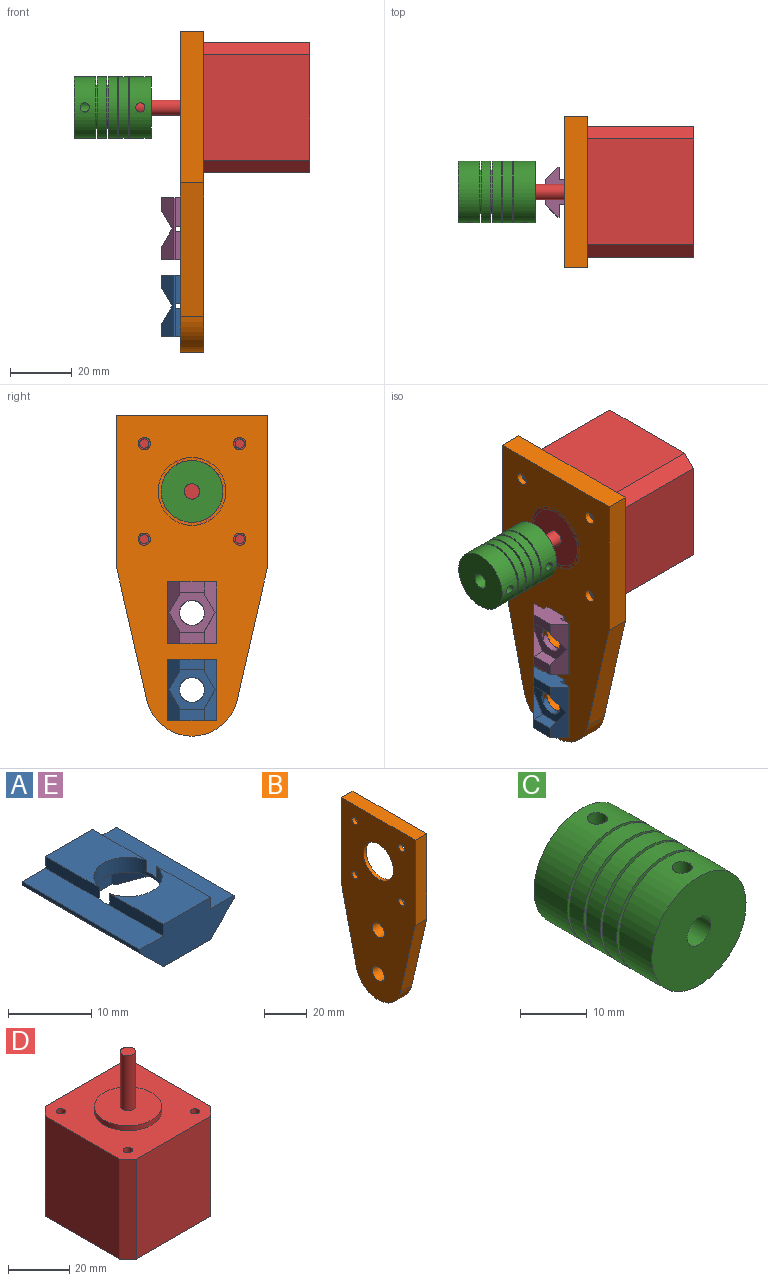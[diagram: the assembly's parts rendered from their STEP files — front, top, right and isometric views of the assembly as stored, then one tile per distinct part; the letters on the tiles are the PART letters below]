
ASSEMBLY  parts=5 mates=4
PART A: 24 faces, bbox 16x20x6.2 mm
  f0: plane 20x0.5mm, normal (-1,0,0), area 10mm2, adj f2,f3,f17,f23
  f1: plane 20x0.5mm, normal (1,0,0), area 10mm2, adj f2,f3,f20,f22
  f2: plane 16x6.2mm, normal (0,1,0), area 69.6mm2, adj f0,f1,f7,f10,f16,f17,f19,f20
  f3: plane 16x6.2mm, normal (0,-1,0), area 69.6mm2, adj f0,f1,f6,f9,f17,f18,f20,f21
  f4: plane 6.5x4mm, normal (-0.87,-0.5,0), area 17.7mm2, adj f5,f7,f14,f15,f22
  f5: plane 6.5x4mm, normal (-0.87,0.5,0), area 17.7mm2, adj f4,f6,f11,f15,f22
  f6: plane 8x3.93mm, normal (0,0,-1), area 28.1mm2, adj f3,f5,f11,f12,f22,f23
  f7: plane 8x3.93mm, normal (0,0,-1), area 28.1mm2, adj f2,f4,f13,f14,f22,f23
  f8: cylinder r=4.1mm len=8.2mm, axis (0,0,-1), area 50.5mm2, adj f9,f10,f15,f16,f17,f18,f19,f20
  f9: plane 9.1x8mm, normal (0,0,1), area 53.7mm2, adj f3,f8,f18,f21
  f10: plane 9.1x8mm, normal (0,0,1), area 53.7mm2, adj f2,f8,f16,f19
  f11: plane 7.51x4mm, normal (0,1,0), area 30mm2, adj f5,f6,f12,f15
  f12: plane 6.5x4mm, normal (0.87,0.5,0), area 17.7mm2, adj f6,f11,f13,f15,f23
  f13: plane 6.5x4mm, normal (0.87,-0.5,0), area 17.7mm2, adj f7,f12,f14,f15,f23
  f14: plane 7.51x4mm, normal (0,-1,0), area 30mm2, adj f4,f7,f13,f15
  f15: plane 15.01x13mm, normal (0,0,-1), area 93.5mm2, adj f4,f5,f8,f11,f12,f13,f14
  f16: plane 9.1x1.7mm, normal (-1,0,0), area 15.5mm2, adj f2,f8,f10,f17
  f17: plane 20x4mm, normal (0,0,1), area 79.9mm2, adj f0,f2,f3,f8,f16,f18
  f18: plane 9.1x1.7mm, normal (-1,0,0), area 15.5mm2, adj f3,f8,f9,f17
  f19: plane 9.1x1.7mm, normal (1,0,0), area 15.5mm2, adj f2,f8,f10,f20
  f20: plane 20x4mm, normal (0,0,1), area 79.9mm2, adj f1,f2,f3,f8,f19,f21
  f21: plane 9.1x1.7mm, normal (1,0,0), area 15.5mm2, adj f3,f8,f9,f20
  f22: plane 20x4mm, normal (0.71,0,-0.71), area 83mm2, adj f1,f2,f3,f4,f5,f6,f7
  f23: plane 20x4mm, normal (-0.71,0,-0.71), area 83mm2, adj f0,f2,f3,f6,f7,f12,f13
PART B: 20 faces, bbox 7.5x49x103.9 mm
  f0: plane 43x43mm, normal (1,0,0), area 1484.6mm2, adj f7,f8,f9,f10,f11,f15,f16,f17
  f1: plane 49x7.5mm, normal (0,-1,0), area 367.5mm2, adj f2,f12,f14,f19
  f2: plane 43.19x9.88mm, normal (0,-0.97,-0.22), area 332.3mm2, adj f1,f3,f14,f19
  f3: cylinder r=15mm len=29.25mm, axis (1,0,0), area 302.8mm2, adj f2,f4,f14,f19
  f4: plane 43.19x9.88mm, normal (0,0.97,-0.22), area 332.3mm2, adj f3,f5,f14,f19
  f5: plane 49x7.5mm, normal (0,1,0), area 367.5mm2, adj f4,f12,f14,f19
  f6: cylinder r=4mm len=8mm, axis (1,0,0), area 188.5mm2, adj f14,f19
  f7: cylinder r=2mm len=4mm, axis (1,0,0), area 25.1mm2, adj f0,f14
  f8: cylinder r=2mm len=4mm, axis (1,0,0), area 25.1mm2, adj f0,f14
  f9: cylinder r=2mm len=4mm, axis (1,0,0), area 25.1mm2, adj f0,f14
  f10: cylinder r=2mm len=4mm, axis (1,0,0), area 25.1mm2, adj f0,f14
  f11: cylinder r=10mm len=20mm, axis (1,0,0), area 125.7mm2, adj f0,f14
  f12: plane 49x7.5mm, normal (0,0,1), area 367.5mm2, adj f1,f5,f14,f19
  f13: cylinder r=4mm len=8mm, axis (1,0,0), area 188.5mm2, adj f14,f19
  f14: plane 103.85x49mm, normal (-1,0,0), area 3879.9mm2, adj f1,f2,f3,f4,f5,f6,f7,f8
  f15: plane 43x5.5mm, normal (0,0,1), area 236.5mm2, adj f0,f16,f18,f19
  f16: plane 43x5.5mm, normal (0,1,0), area 236.5mm2, adj f0,f15,f17,f19
  f17: plane 43x5.5mm, normal (0,0,-1), area 236.5mm2, adj f0,f16,f18,f19
  f18: plane 43x5.5mm, normal (0,-1,0), area 236.5mm2, adj f0,f15,f17,f19
  f19: plane 103.85x49mm, normal (1,0,0), area 2395.3mm2, adj f1,f2,f3,f4,f5,f6,f12,f13
PART C: 22 faces, bbox 20x25x20 mm
  f0: cylinder r=10mm len=20mm, axis (0,1,0), area 435.3mm2, adj f4,f6,f7
  f1: cylinder r=2.5mm len=25mm, axis (0,1,0), area 377.9mm2, adj f3,f4,f5,f6
  f2: cylinder r=10mm len=20mm, axis (0,1,0), area 430.1mm2, adj f3,f5,f11
  f3: plane 20x20mm, normal (0,-1,0), area 294.5mm2, adj f1,f2
  f4: plane 20x20mm, normal (0,1,0), area 294.5mm2, adj f0,f1
  f5: cylinder r=1.5mm len=8mm, axis (0,0,-1), area 72.4mm2, adj f1,f2
  f6: cylinder r=1.5mm len=8mm, axis (0,0,-1), area 72.4mm2, adj f0,f1
  f7: plane 20x20mm, normal (0,-1,0), area 154.1mm2, adj f0,f9
  f8: plane 20x20mm, normal (0,1,0), area 154.1mm2, adj f9,f13
  f9: cylinder r=7.14mm len=14.28mm, axis (0,1,0), area 22.4mm2, adj f7,f8
  f10: plane 20x20mm, normal (0,-1,0), area 154.1mm2, adj f12,f17
  f11: plane 20x20mm, normal (0,1,0), area 154.1mm2, adj f2,f12
  f12: cylinder r=7.14mm len=14.28mm, axis (0,1,0), area 22.4mm2, adj f10,f11
  f13: cylinder r=10mm len=20mm, axis (0,1,0), area 188.5mm2, adj f8,f14
  f14: plane 20x20mm, normal (0,-1,0), area 154.1mm2, adj f13,f16
  f15: plane 20x20mm, normal (0,1,0), area 154.1mm2, adj f16,f21
  f16: cylinder r=7.14mm len=14.28mm, axis (0,1,0), area 22.4mm2, adj f14,f15
  f17: cylinder r=10mm len=20mm, axis (0,1,0), area 188.5mm2, adj f10,f19
  f18: plane 20x20mm, normal (0,-1,0), area 154.1mm2, adj f20,f21
  f19: plane 20x20mm, normal (0,1,0), area 154.1mm2, adj f17,f20
  f20: cylinder r=7.14mm len=14.28mm, axis (0,1,0), area 22.4mm2, adj f18,f19
  f21: cylinder r=10mm len=20mm, axis (0,1,0), area 188.5mm2, adj f15,f18
PART D: 22 faces, bbox 42.3x42.3x64 mm
  f0: plane 40x34.3mm, normal (-1,0,0), area 1372mm2, adj f4,f5,f20,f21
  f1: plane 40x34.3mm, normal (0,-1,0), area 1372mm2, adj f4,f5,f19,f20
  f2: plane 40x34.3mm, normal (1,0,0), area 1372mm2, adj f4,f5,f18,f19
  f3: plane 40x34.3mm, normal (0,1,0), area 1372mm2, adj f4,f5,f18,f21
  f4: plane 42.3x42.3mm, normal (0,0,-1), area 1757.3mm2, adj f0,f1,f2,f3,f18,f19,f20,f21
  f5: plane 42.3x42.3mm, normal (0,0,1), area 1348.9mm2, adj f0,f1,f2,f3,f6,f10,f12,f14
  f6: cylinder r=11mm len=22mm, axis (0,0,-1), area 138.2mm2, adj f5,f7
  f7: plane 22x22mm, normal (0,0,1), area 360.5mm2, adj f6,f9
  f8: plane 5x5mm, normal (0,0,1), area 19.6mm2, adj f9
  f9: cylinder r=2.5mm len=22mm, axis (0,0,-1), area 345.6mm2, adj f7,f8
  f10: cylinder r=1.5mm len=4.5mm, axis (0,0,1), area 42.4mm2, adj f5,f11
  f11: plane 3x3mm, normal (0,0,1), area 7.1mm2, adj f10
  f12: cylinder r=1.5mm len=4.5mm, axis (0,0,1), area 42.4mm2, adj f5,f13
  f13: plane 3x3mm, normal (0,0,1), area 7.1mm2, adj f12
  f14: cylinder r=1.5mm len=4.5mm, axis (0,0,1), area 42.4mm2, adj f5,f15
  f15: plane 3x3mm, normal (0,0,1), area 7.1mm2, adj f14
  f16: cylinder r=1.5mm len=4.5mm, axis (0,0,1), area 42.4mm2, adj f5,f17
  f17: plane 3x3mm, normal (0,0,1), area 7.1mm2, adj f16
  f18: plane 40x4mm, normal (0.71,0.71,0), area 226.3mm2, adj f2,f3,f4,f5
  f19: plane 40x4mm, normal (0.71,-0.71,0), area 226.3mm2, adj f1,f2,f4,f5
  f20: plane 40x4mm, normal (-0.71,-0.71,0), area 226.3mm2, adj f0,f1,f4,f5
  f21: plane 40x4mm, normal (-0.71,0.71,0), area 226.3mm2, adj f0,f3,f4,f5
PART E: same geometry as A
PLACE A rot(axis=(0.58,0.58,0.58),120deg) t=(-21.3,-49.3,-57.08)mm
PLACE B t=(-17.1,-49.3,7.27)mm
PLACE C rot(axis=(0.58,-0.58,0.58),120deg) t=(-53.6,-49.3,7.27)mm
PLACE D rot(axis=(0.71,0,-0.71),180deg) t=(-17.1,-49.3,7.27)mm
PLACE E rot(axis=(0.58,0.58,0.58),120deg) t=(-21.3,-49.3,-32.08)mm
MATE fastened B.f13 <-> A.f8  axis (1,0,0) through (-19.1,-49.3,-57.08)mm
MATE revolute C.f1 <-> D.f9  axis (-1,0,0) through (-41.1,-49.3,7.27)mm
MATE fastened D.f6 <-> B.f11  axis (-1,0,0) through (-17.1,-49.3,7.27)mm
MATE fastened B.f6 <-> E.f8  axis (-1,0,0) through (-19.1,-49.3,-32.08)mm
